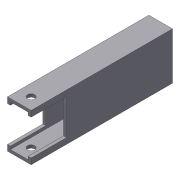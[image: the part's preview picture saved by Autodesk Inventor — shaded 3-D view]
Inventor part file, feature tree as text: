
AUTODESK INVENTOR PART (.ipt)
format: ipt  version: 2012 (Build 160160000, 160)  size: 99,840 bytes
history: native  units: in
note: dims shown in document units (in); Inventor stores cm internally (conversion verified against a paired STEP export)
features: extrude x3, sketch x3, shell x1
ambient origin geometry x8: Origin, YZ Plane, XZ Plane, XY Plane, X Axis, Y Axis, Z Axis, Center Point
bodies: Solid1 (feature_tree)
feature tree (7):
  extrude  "Extrusion1"  Depth=2.0in
  shell  "Shell1"  Thickness=6.0in
  extrude  "Extrusion4"  Depth=0.25in
  extrude  "Extrusion5"  Depth=1.5in
  sketch  "Sketch1"  dims[d0=1.0in d1=2.0in d2=6.0in d3=0.0in]
  sketch  "Sketch4"  dims[d4=0.125in d15=0.25in]
  sketch  "Sketch5"  dims[d16=0.25in d17=1.5in d18=6.0in d19=0.0in d20=0.3125in d21=0.5in d22=0.5in d23=6.0in d24=0.0in]
